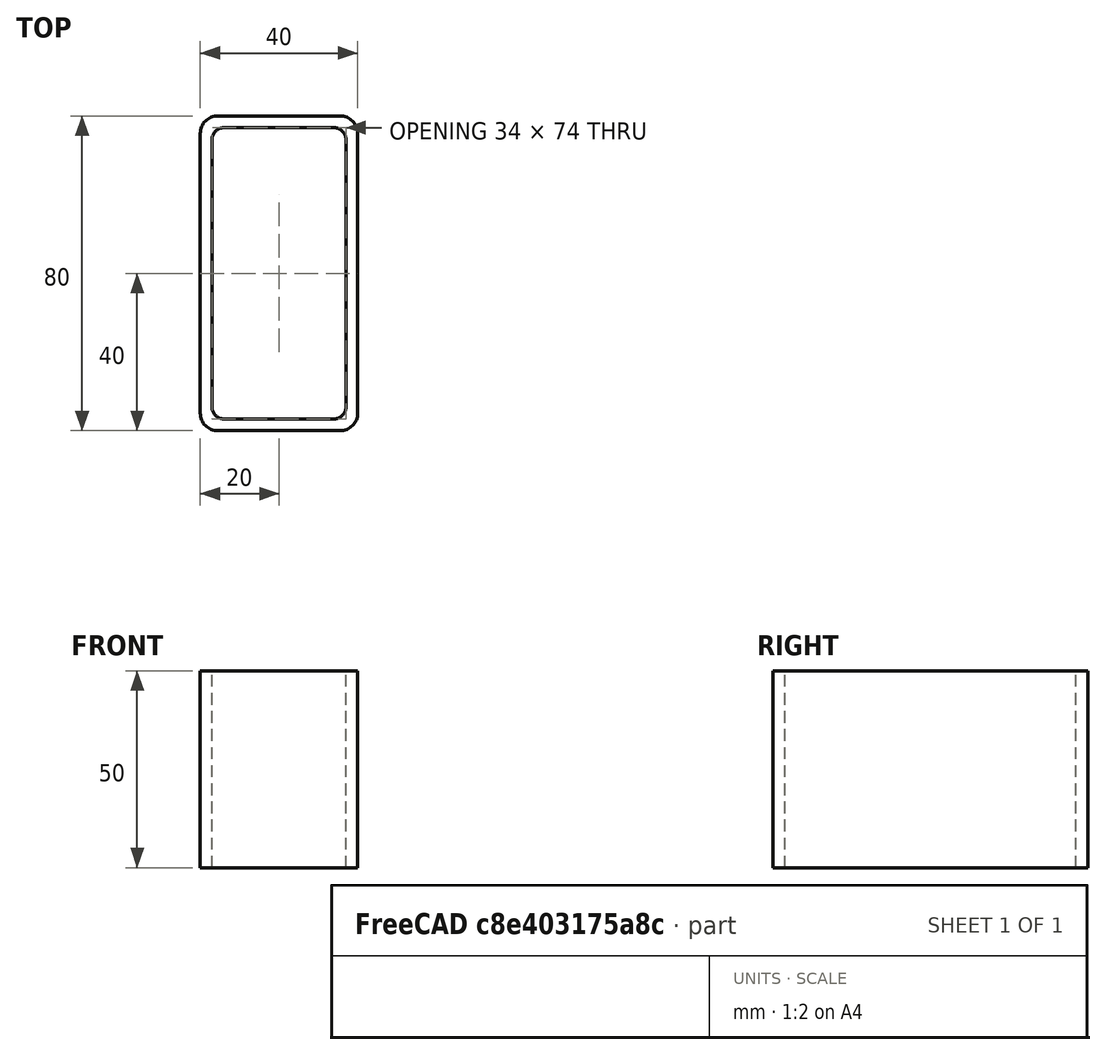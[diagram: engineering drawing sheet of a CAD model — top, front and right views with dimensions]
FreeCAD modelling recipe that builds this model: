
FCSTD DOCUMENT  (FreeCAD 0.15R4671 (Git))
Label: Rectangular hollow section 80x40x3 EN10219 S235JRH
License: All rights reserved
LicenseURL: http://en.wikipedia.org/wiki/All_rights_reserved
objects: Sketcher::SketchObject×1, Part::Extrusion×1
note: 2 computed .brp shape members not serialized (recipe doc carries the construction recipe); baked Part::Feature solids carry a one-line shape summary decoded from their .brp

FEATURE [Sketcher::SketchObject] Sketch
  sketch-geometry (16):
    g0: LineSegment StartX=-14 StartY=37 StartZ=0 EndX=14 EndY=37 EndZ=0
    g1: LineSegment StartX=17 StartY=34 StartZ=0 EndX=17 EndY=-34 EndZ=0
    g2: LineSegment StartX=14 StartY=-37 StartZ=0 EndX=-14 EndY=-37 EndZ=0
    g3: LineSegment StartX=-17 StartY=-34 StartZ=0 EndX=-17 EndY=34 EndZ=0
    g4: LineSegment StartX=-15.5 StartY=40 StartZ=0 EndX=15.5 EndY=40 EndZ=0
    g5: LineSegment StartX=20 StartY=35.5 StartZ=0 EndX=20 EndY=-35.5 EndZ=0
    g6: LineSegment StartX=15.5 StartY=-40 StartZ=0 EndX=-15.5 EndY=-40 EndZ=0
    g7: LineSegment StartX=-20 StartY=-35.5 StartZ=0 EndX=-20 EndY=35.5 EndZ=0
    g8: ArcOfCircle CenterX=-14 CenterY=34 CenterZ=0 NormalX=0 NormalY=0 NormalZ=1 Radius=3 StartAngle=1.5708 EndAngle=3.14159
    g9: ArcOfCircle CenterX=14 CenterY=34 CenterZ=0 NormalX=0 NormalY=0 NormalZ=1 Radius=3 StartAngle=0 EndAngle=1.5708
    g10: ArcOfCircle CenterX=14 CenterY=-34 CenterZ=0 NormalX=0 NormalY=0 NormalZ=1 Radius=3 StartAngle=4.71239 EndAngle=6.28319
    g11: ArcOfCircle CenterX=-14 CenterY=-34 CenterZ=0 NormalX=0 NormalY=0 NormalZ=1 Radius=3 StartAngle=3.14159 EndAngle=4.71239
    g12: ArcOfCircle CenterX=15.5 CenterY=35.5 CenterZ=0 NormalX=0 NormalY=0 NormalZ=1 Radius=4.5 StartAngle=0 EndAngle=1.5708
    g13: ArcOfCircle CenterX=15.5 CenterY=-35.5 CenterZ=0 NormalX=0 NormalY=0 NormalZ=1 Radius=4.5 StartAngle=4.71239 EndAngle=6.28319
    g14: ArcOfCircle CenterX=-15.5 CenterY=-35.5 CenterZ=0 NormalX=0 NormalY=0 NormalZ=1 Radius=4.5 StartAngle=3.14159 EndAngle=4.71239
    g15: ArcOfCircle CenterX=-15.5 CenterY=35.5 CenterZ=0 NormalX=0 NormalY=0 NormalZ=1 Radius=4.5 StartAngle=1.5708 EndAngle=3.14159
  constraints (36):
    c: Horizontal(g2)
    c: Vertical(g3)
    c: Horizontal(g6)
    c: Vertical(g7)
    c: Tangent(g3,g8) = 1.5708
    c: Tangent(g0,g8) = 1.5708
    c: Tangent(g0,g9) = 1.5708
    c: Tangent(g1,g9) = 1.5708
    c: Tangent(g1,g10) = 1.5708
    c: Tangent(g2,g10) = 1.5708
    c: Tangent(g2,g11) = 1.5708
    c: Tangent(g3,g11) = 1.5708
    c: Tangent(g4,g12) = 1.5708
    c: Tangent(g5,g12) = 1.5708
    c: Tangent(g5,g13) = 1.5708
    c: Tangent(g6,g13) = 1.5708
    c: Tangent(g6,g14) = 1.5708
    c: Tangent(g7,g14) = 1.5708
    c: Tangent(g7,g15) = 1.5708
    c: Tangent(g4,g15) = 1.5708
    c: Equal(g9,g8)
    c: Equal(g9,g11)
    c: Equal(g9,g10)
    c: Equal(g12,g15)
    c: Equal(g12,g14)
    c: Equal(g12,g13)
    c: Symmetric(g4,g6,g-1)
    c: Symmetric(g7,g5,g-2)
    c: DistanceY(g4,g6) = -80
    c: DistanceX(g7,g5) = 40
    c: Symmetric(g3,g1,g-2)
    c: Symmetric(g0,g2,g-1)
    c: DistanceY(g0,g4) = 3
    c: DistanceX(g5,g1) = -3
    c: Radius(g9) = 3
    c: Radius(g12) = 4.5
FEATURE [Part::Extrusion] Extrude  label="Rectangular hollow section 80x40x3 EN10219 S235JRH"
  Base = -> Sketch
  Dir = (0,0,50)
  Solid = true
